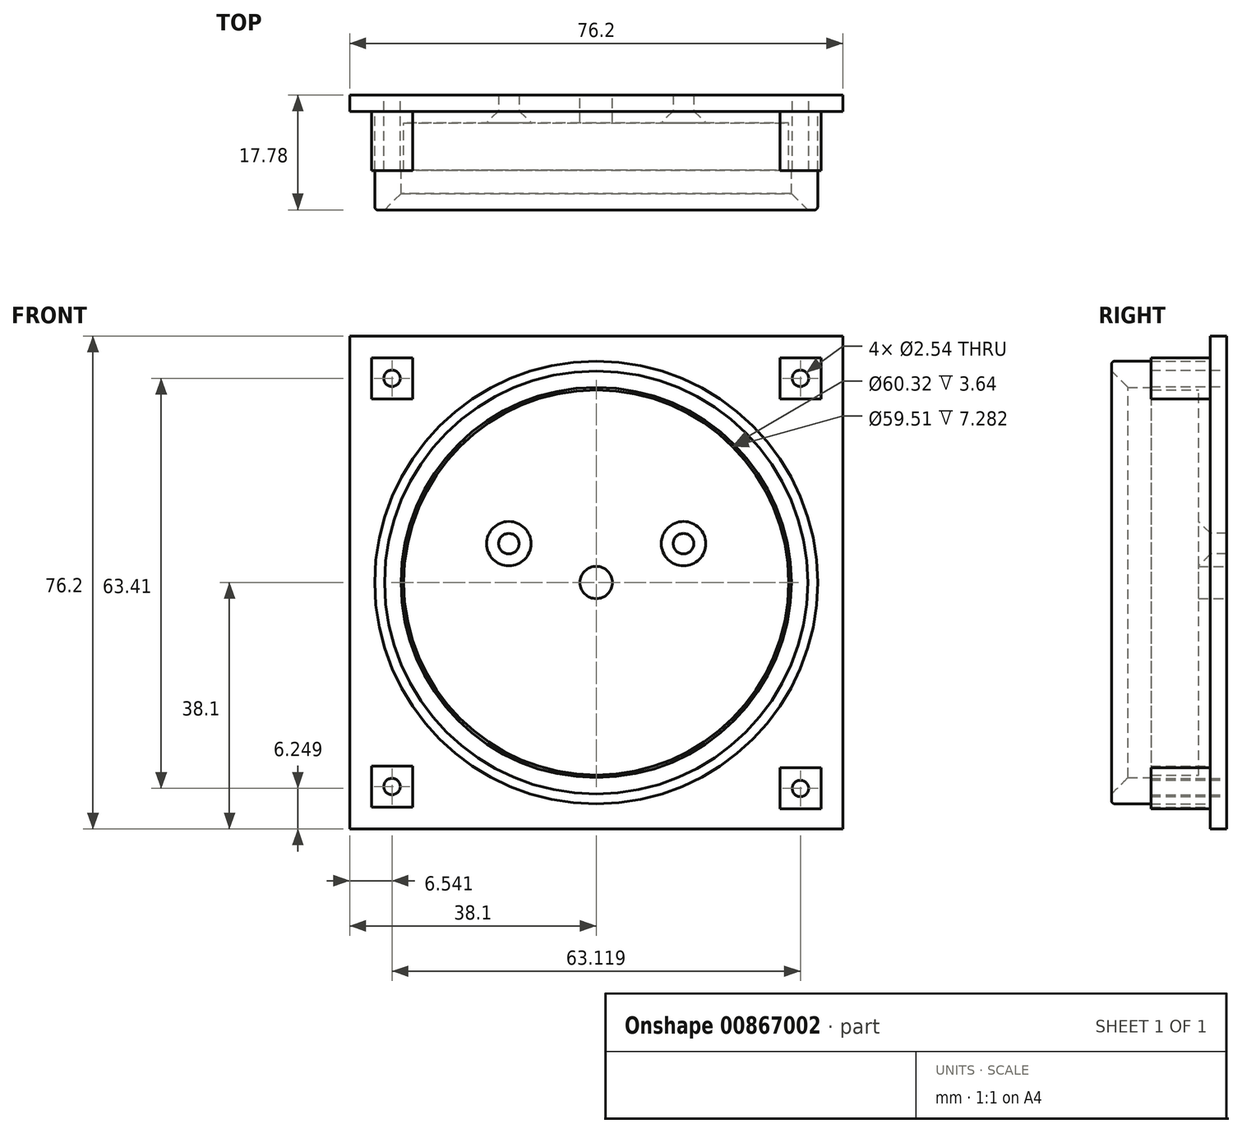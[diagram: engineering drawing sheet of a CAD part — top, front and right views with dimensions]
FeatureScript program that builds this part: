
annotation { "Feature Type Name" : "Feature", "Feature Type Description" : "" }
export const myFeature = defineFeature(function(context is Context, id is Id, definition is map)
    precondition{}
    {
        {
            var Q0;
            Q0=qCreatedBy(makeId("Front.planeOp"),FACE);
            var sketch = newSketch(context, id + "F0", { "sketchPlane" : qUnion([Q0])});
            skCircle(sketch, "E0", {"center": v(0, 0) * mm, "radius": 30.16 * mm});
            skLineSegment(sketch, "E1.bottom", {"start": v(38.1, 38.1) * mm, "end": v(-38.1, 38.1) * mm});
            skLineSegment(sketch, "E1.top", {"start": v(38.1, -38.1) * mm, "end": v(-38.1, -38.1) * mm});
            skLineSegment(sketch, "E1.left", {"start": v(38.1, 38.1) * mm, "end": v(38.1, -38.1) * mm});
            skLineSegment(sketch, "E1.right", {"start": v(-38.1, 38.1) * mm, "end": v(-38.1, -38.1) * mm});
            skPoint(sketch, "E2", {"position": v(-31.56, 31.56) * mm});
            skPoint(sketch, "E3", {"position": v(31.56, 31.56) * mm});
            skPoint(sketch, "E4", {"position": v(31.56, -31.85) * mm});
            skPoint(sketch, "E5", {"position": v(-31.56, -31.56) * mm});
            skLineSegment(sketch, "E6.bottom", {"start": v(-28.38, 34.73) * mm, "end": v(-34.73, 34.73) * mm});
            skLineSegment(sketch, "E6.top", {"start": v(-28.38, 28.38) * mm, "end": v(-34.73, 28.38) * mm});
            skLineSegment(sketch, "E6.left", {"start": v(-28.38, 34.73) * mm, "end": v(-28.38, 28.38) * mm});
            skLineSegment(sketch, "E6.right", {"start": v(-34.73, 34.73) * mm, "end": v(-34.73, 28.38) * mm});
            skLineSegment(sketch, "E7.bottom", {"start": v(34.73, 34.73) * mm, "end": v(28.38, 34.73) * mm});
            skLineSegment(sketch, "E7.top", {"start": v(34.73, 28.38) * mm, "end": v(28.38, 28.38) * mm});
            skLineSegment(sketch, "E7.left", {"start": v(34.73, 34.73) * mm, "end": v(34.73, 28.38) * mm});
            skLineSegment(sketch, "E7.right", {"start": v(28.38, 34.73) * mm, "end": v(28.38, 28.38) * mm});
            skLineSegment(sketch, "E8.bottom", {"start": v(34.73, -28.68) * mm, "end": v(28.38, -28.68) * mm});
            skLineSegment(sketch, "E8.top", {"start": v(34.73, -35.03) * mm, "end": v(28.38, -35.03) * mm});
            skLineSegment(sketch, "E8.left", {"start": v(34.73, -28.68) * mm, "end": v(34.73, -35.03) * mm});
            skLineSegment(sketch, "E8.right", {"start": v(28.38, -28.68) * mm, "end": v(28.38, -35.03) * mm});
            skLineSegment(sketch, "E9.bottom", {"start": v(-28.38, -28.38) * mm, "end": v(-34.73, -28.38) * mm});
            skLineSegment(sketch, "E9.top", {"start": v(-28.38, -34.73) * mm, "end": v(-34.73, -34.73) * mm});
            skLineSegment(sketch, "E9.left", {"start": v(-28.38, -28.38) * mm, "end": v(-28.38, -34.73) * mm});
            skLineSegment(sketch, "E9.right", {"start": v(-34.73, -28.38) * mm, "end": v(-34.73, -34.73) * mm});
            skSolve(sketch);
        }
        {
            var Q0;
            Q0=makeQuery(id+"F0.imprint","IMPRINT",FACE,{"disambiguationData":[TD([[makeQuery(id+"F0.imprint","IMPRINT",EDGE,{"derivedFrom":sQuery(id+"F0.wireOp",EDGE,"E0")}),1.0]])]});
            extrude(context, id + "F1", {"entities" : qUnion([Q0]), "depth" : 4.32 * mm, "offsetDistance" : 25.4 * mm});
        }
        {
            var Q0;
            Q0=qCreatedBy(makeId("Front.planeOp"),FACE);
            var sketch = newSketch(context, id + "F2", { "sketchPlane" : qUnion([Q0])});
            skCircle(sketch, "E10", {"center": v(0, 0) * mm, "radius": 30.16 * mm});
            skCircle(sketch, "E11", {"center": v(0, 0) * mm, "radius": 34.23 * mm});
            skSolve(sketch);
        }
        {
            var Q0;
            Q0=qSketchRegion(id+"F2",true);
            extrude(context, id + "F3", {"entities" : qUnion([Q0]), "operationType" : NewBodyOperationType.ADD, "depth" : 17.78 * mm, "offsetDistance" : 25.4 * mm});
        }
        {
            var Q0;
            Q0=makeQuery(id+"F0.imprint","IMPRINT",FACE,{"disambiguationData":[TD([[makeQuery(id+"F0.imprint","IMPRINT",EDGE,{"derivedFrom":sQuery(id+"F0.wireOp",EDGE,"E0")}),-1.0]])]});
            extrude(context, id + "F4", {"entities" : qUnion([Q0]), "operationType" : NewBodyOperationType.ADD, "depth" : 2.54 * mm, "offsetDistance" : 25.4 * mm});
        }
        {
            var Q0;
            Q0=makeQuery(id+"F0.imprint","IMPRINT",FACE,{"disambiguationData":[TD([[makeQuery(id+"F0.imprint","IMPRINT",EDGE,{"derivedFrom":sQuery(id+"F0.wireOp",EDGE,"E9.bottom")}),1.0]])]});
            var Q1;
            Q1=makeQuery(id+"F0.imprint","IMPRINT",FACE,{"disambiguationData":[TD([[makeQuery(id+"F0.imprint","IMPRINT",EDGE,{"derivedFrom":sQuery(id+"F0.wireOp",EDGE,"E6.bottom")}),1.0]])]});
            var Q2;
            Q2=makeQuery(id+"F0.imprint","IMPRINT",FACE,{"disambiguationData":[TD([[makeQuery(id+"F0.imprint","IMPRINT",EDGE,{"derivedFrom":sQuery(id+"F0.wireOp",EDGE,"E7.bottom")}),1.0]])]});
            var Q3;
            Q3=makeQuery(id+"F0.imprint","IMPRINT",FACE,{"disambiguationData":[TD([[makeQuery(id+"F0.imprint","IMPRINT",EDGE,{"derivedFrom":sQuery(id+"F0.wireOp",EDGE,"E8.bottom")}),1.0]])]});
            extrude(context, id + "F5", {"entities" : qUnion([Q0, Q1, Q2, Q3]), "operationType" : NewBodyOperationType.ADD, "depth" : 11.68 * mm, "offsetDistance" : 25.4 * mm});
        }
        {
            var Q0;
            Q0=sQuery(id+"F0.wireOp",VERTEX,"E2");
            var Q1;
            Q1=sQuery(id+"F0.wireOp",VERTEX,"E3");
            var Q2;
            Q2=sQuery(id+"F0.wireOp",VERTEX,"E5");
            var Q3;
            Q3=sQuery(id+"F0.wireOp",VERTEX,"E4");
            var Q4;
            Q4=makeQuery(id+"F1.opExtrude","SWEPT_BODY",BODY,{"disambiguationData":[OSD([sQuery(id+"F0.wireOp",EDGE,"E0"),sQuery(id+"F0.wireOp",EDGE,"mUU7OhdX-XNa0-4Drs-y0eB-kvNcseM0QuPt"),sQuery(id+"F0.wireOp",EDGE,"VLppaxhi-9gsj-CoUi-4eyW-4ZfSdwgNkN1v"),sQuery(id+"F0.wireOp",EDGE,"52aOqeBn-3A06-FGgB-2pqV-L4Iadewni0vA"),sQuery(id+"F0.wireOp",EDGE,"DvhnZx25-jBlL-CNyz-VQNl-D04Q6eJg0ANY.bottom"),sQuery(id+"F0.wireOp",EDGE,"DvhnZx25-jBlL-CNyz-VQNl-D04Q6eJg0ANY.top")])]});
            hole(context, id + "F6", {"style" : HoleStyle.SIMPLE, "endStyle" : HoleEndStyle.THROUGH, "oppositeDirection" : true, "holeDiameter" : 2.54 * mm, "majorDiameter" : 6.35 * mm, "isTappedThrough" : true, "tappedDepth" : 12.7 * mm, "tapClearance" : 3, "locations" : qUnion([Q0, Q1, Q2, Q3]), "scope" : qUnion([Q4])});
        }
        {
            var Q0;
            Q0=sQuery(id+"F0.wireOp",VERTEX,"E0.center");
            var Q1;
            Q1=makeQuery(id+"F1.opExtrude","SWEPT_BODY",BODY,{"disambiguationData":[OSD([sQuery(id+"F0.wireOp",EDGE,"E0")])]});
            hole(context, id + "F7", {"style" : HoleStyle.SIMPLE, "endStyle" : HoleEndStyle.THROUGH, "oppositeDirection" : true, "holeDiameter" : 5 * mm, "majorDiameter" : 5 * mm, "isTappedThrough" : true, "tappedDepth" : 12 * mm, "tapClearance" : 3, "locations" : qUnion([Q0]), "scope" : qUnion([Q1])});
        }
        {
            var Q0;
            Q0=makeQuery(id+"F1.opExtrude","CAP_FACE",FACE,{"disambiguationData":[OSD([sQuery(id+"F0.wireOp",EDGE,"E0")])],"isStart":false});
            var sketch = newSketch(context, id + "F8", { "sketchPlane" : qUnion([Q0])});
            skPoint(sketch, "E12", {"position": v(-13.5, 6) * mm});
            skPoint(sketch, "E13", {"position": v(13.5, 6) * mm});
            skSolve(sketch);
        }
        {
            var Q0;
            Q0=sQuery(id+"F8.wireOp",VERTEX,"E12");
            var Q1;
            Q1=sQuery(id+"F8.wireOp",VERTEX,"E13");
            var Q2;
            Q2=makeQuery(id+"F1.opExtrude","SWEPT_BODY",BODY,{"disambiguationData":[OSD([sQuery(id+"F0.wireOp",EDGE,"E0")])]});
            hole(context, id + "F9", {"style" : HoleStyle.C_SINK, "endStyle" : HoleEndStyle.THROUGH, "holeDiameter" : 3.17 * mm, "cSinkDiameter" : 6.86 * mm, "cSinkAngle" : 90 * degree, "majorDiameter" : 5 * mm, "isTappedThrough" : true, "tappedDepth" : 12 * mm, "tapClearance" : 3, "locations" : qUnion([Q0, Q1]), "scope" : qUnion([Q2])});
        }
        {
            var Q0;
            Q0=makeQuery(id+"F3.opExtrude","CAP_EDGE",EDGE,{"disambiguationData":[OSD([sQuery(id+"F2.wireOp",EDGE,"E10")])],"isStart":false});
            chamfer(context, id + "F10", {"entities" : qUnion([Q0]), "width" : 2.54 * mm, "tangentPropagation" : true});
        }
        {
            var Q0;
            Q0=makeQuery(id+"F3.opExtrude","CAP_EDGE",EDGE,{"disambiguationData":[OSD([sQuery(id+"F2.wireOp",EDGE,"E11")])],"isStart":false});
            fillet(context, id + "F11", {"entities" : qUnion([Q0]), "radius" : .508 * mm, "tangentPropagation" : true, "allowEdgeOverflow" : false});
        }
        {
            var Q0;
            Q0=qCreatedBy(makeId("Front.planeOp"),FACE);
            var sketch = newSketch(context, id + "F12", { "sketchPlane" : qUnion([Q0])});
            skCircle(sketch, "E14", {"center": v(0, 0) * mm, "radius": 30.16 * mm});
            skCircle(sketch, "E15", {"center": v(0, 0) * mm, "radius": 29.76 * mm});
            skSolve(sketch);
        }
        {
            var Q0;
            Q0=qSketchRegion(id+"F12",true);
            extrude(context, id + "F13", {"entities" : qUnion([Q0]), "operationType" : NewBodyOperationType.ADD, "depth" : 11.6 * mm, "offsetDistance" : 25 * mm});
        }
    });
